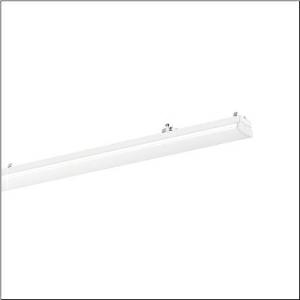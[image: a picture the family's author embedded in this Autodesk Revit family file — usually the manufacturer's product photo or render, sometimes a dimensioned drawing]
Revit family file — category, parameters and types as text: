
# Revit family: licross_21_recessed_opal_mo_52te1ddv495g
name_source: partatom
category: Lighting Fixtures
units: mm (PartAtom-declared; Revit-internal decimal feet)

## family parameters
Cut with Voids When Loaded = No
Host = Face
Light Source = No
Part Type = Normal
Room Calculation Point = No
Round Connector Dimension = Use Diameter
Shared = No

## types (1)
- --- (1 x LED, 9500 lm, 53.6 W, 4000K)
    Apparent Load = 54 VA
    CIE Flux Codes = 44 73 91 87 100
    Color Rendering = 80
    Color Temperature = 4000K
    Default Elevation = 1800 mm
    Description = Licross 21 recessed opal MO, luminaire insert, of sheet steel, galvanised, coil coated, white, length: 2.250mm, width: 66mm, height: 67mm, LED rated luminous flux: 9.500lm, light colour: 840, SDCM (Standard Deviation of Colour Matching)MacAdam ≤ 3 SDCM (initial), control gear: DALI 2, with plug, 5-pole, with phase selection, mains connection: 220..240V, AC, 50/60Hz, rated input power: 54W, internal wiring halogen-free, primary optical cover: cover, of PMMA, light emission: direct with ceiling illumination distribution, primary light characteristic: symmetric, protection rating (complete): IP54, insulation class (complete): insulation class I (protective earthing), certification: CE, ENEC, VDE, UKCA, protection symbol: D if used in an environment with non-conductive dust loads with corresponding accessories, impact resistance: IK06, permissible ambient temperature for indoor applications: -25..+40°C, corresponds to IFS (International Featured Standards) requirements for safety and quality in the food industry, reducing of maximum allowable ambient temperature of 5°C with ceiling mounting, LABS conformity tested according to VDMA 24364:2018-05, The light source and the operating device comply with the requirements of the Ecodesign Regulation (EU) 2019/2020 and are replaceable in accordance with this regulation, packaging unit: 1 piece
    Height = 83 mm
    Lamp = 1 x LED
    Lamp Light Flux = 9500 lm
    Lamp Power = 53.6 W
    Lamp count = 1
    Length = 2250 mm
    Luminous efficacy = 177 lm/W
    Manufacturer = Siteco
    ModVariant = No
    Model = 52TE1DDV495G
    Mounting Place = Ceiling
    Mounting Type = Pendant
    Number of Poles = 1
    OnlyDefault = Yes
    Power Factor = 1
    Product Name = Licross 21 recessed opal MO
    Product group = luminaire insert | ceiling pendant
    ProductGroupID = 901
    Protection Class = Protection class I
    Protection Degree = IP 54
    RLX_Detail_Level = 1
    RLX_Emergency_Light_Flux = 0 lm
    RLX_Emergency_Type = 0
    RLX_Emergency_Type_DB = No
    RlxData = <blob elided: 26633 chars, md5=7284beb6>
    Socket = socket
    Standby Power = 0 W
    System Light Flux = 9500 lm
    System Power = 54 W
    Type Comments = factory setting: luminous flux: 100 % | dim-lin: 254 | 246 mA
    Type Image = l_1313666.jpg
    URL = http://relux.com
    VarID = @adj_072363
    Voltage = 0 V
    Weight = 0.00 kg
    Width = 76 mm

## geometry (parser evidence)
native form markers: Blend x4, Sweep x15
no freeform markers — native parametric forms only
